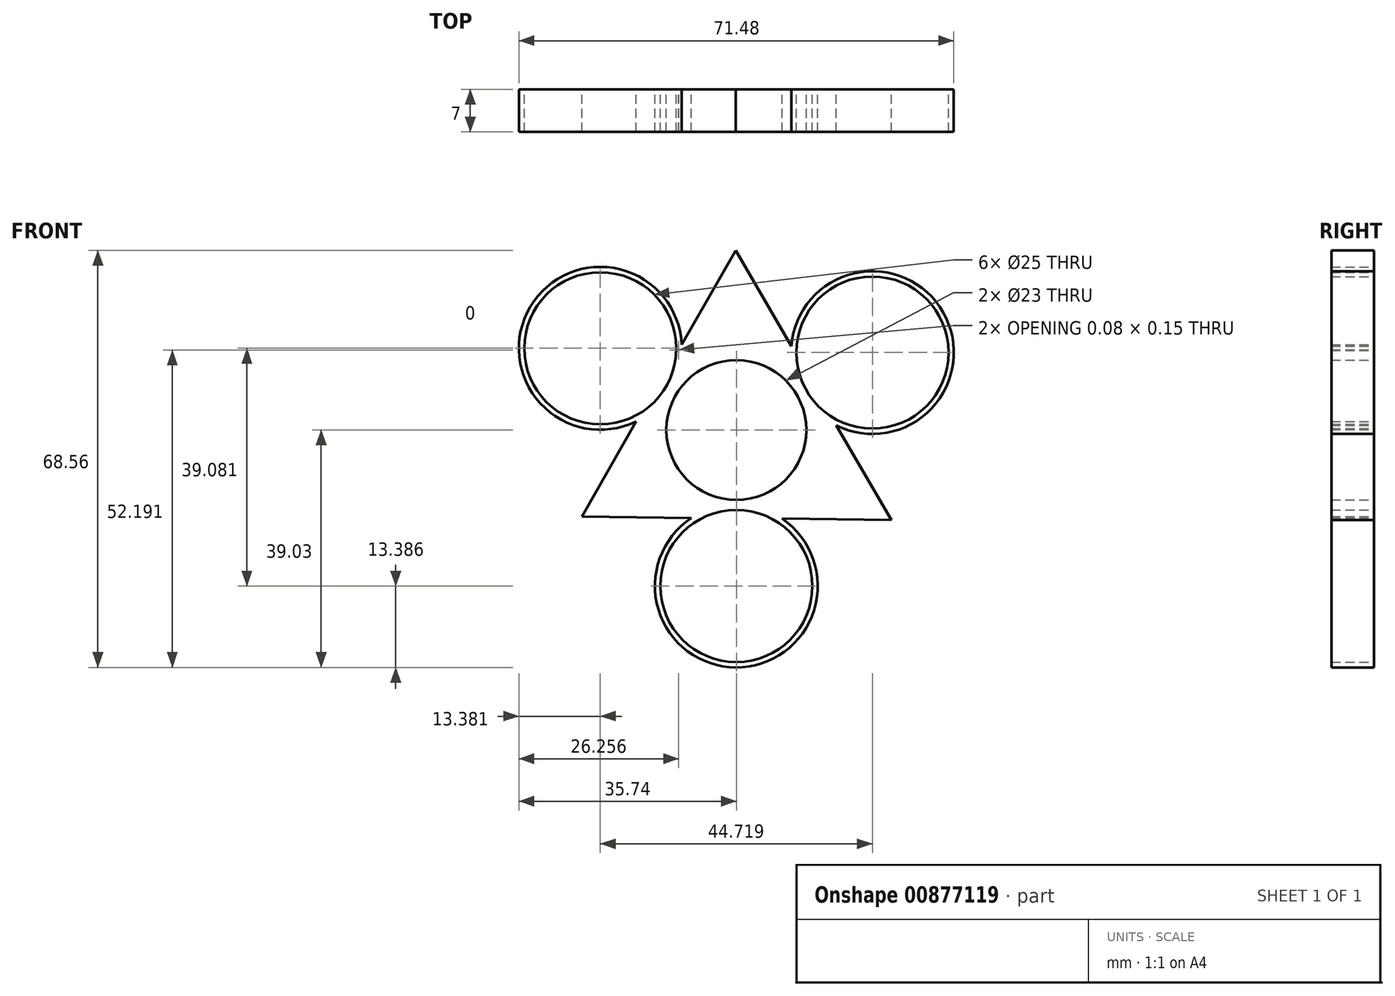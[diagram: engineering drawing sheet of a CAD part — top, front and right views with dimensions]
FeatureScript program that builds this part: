
annotation { "Feature Type Name" : "Feature", "Feature Type Description" : "" }
export const myFeature = defineFeature(function(context is Context, id is Id, definition is map)
    precondition{}
    {
        {
            var Q0;
            Q0=qCreatedBy(makeId("Front.planeOp"),FACE);
            var sketch = newSketch(context, id + "F0", { "sketchPlane" : qUnion([Q0])});
            skPoint(sketch, "E0.0.midPoint", {"position": v(-1.03, 12.4) * mm});
            skPoint(sketch, "E1.orphan", {"position": v(-18.38, 13.22) * mm});
            skPoint(sketch, "E0.0.start.orphan", {"position": v(16.32, 11.57) * mm});
            skCircle(sketch, "E2", {"center": v(0, 0) * mm, "radius": 11.5 * mm});
            skPoint(sketch, "E3.0.midPoint", {"position": v(21.95, 0) * mm});
            skPoint(sketch, "E4.orphan", {"position": v(21.95, 38.02) * mm});
            skPoint(sketch, "E3.0.end.orphan", {"position": v(21.95, -38.02) * mm});
            skPoint(sketch, "E5.0.midPoint", {"position": v(-12.82, 7.67) * mm});
            skPoint(sketch, "E5.1.start.orphan", {"position": v(0.46, 29.87) * mm});
            skPoint(sketch, "E5.0.start.orphan", {"position": v(-26.1, -14.53) * mm});
            skSolve(sketch);
        }
        {
            var Q0;
            Q0=qCreatedBy(makeId("Front.planeOp"),FACE);
            var sketch = newSketch(context, id + "F1", { "sketchPlane" : qUnion([Q0])});
            skPoint(sketch, "E6.0.midPoint", {"position": v(0, 3.19) * mm});
            skPoint(sketch, "E7.orphan", {"position": v(-16.3, -47.78) * mm});
            skPoint(sketch, "E6.1.start.orphan", {"position": v(16.3, 54.15) * mm});
            skPoint(sketch, "E8.orphan", {"position": v(16.3, -28.22) * mm});
            skPoint(sketch, "E6.cCircle.center.orphan", {"position": v(0, 0) * mm});
            skPoint(sketch, "E9.0.midPoint", {"position": v(20.45, 12.84) * mm});
            skPoint(sketch, "E10.center.orphan", {"position": v(40.9, -48.55) * mm});
            skPoint(sketch, "E11.orphan", {"position": v(-0.12, 29.53) * mm});
            skPoint(sketch, "E12.0.midPoint", {"position": v(0, 13.09) * mm});
            skLineSegment(sketch, "E13", {"start": v(122.5, 32.06) * mm, "end": v(120.9, 14.13) * mm});
            skLineSegment(sketch, "E14.0", {"start": v(-22.36, 13.44) * mm, "end": v(22.36, 12.73) * mm});
            skLineSegment(sketch, "E14.1", {"start": v(22.36, 12.73) * mm, "end": v(0, -25.64) * mm});
            skLineSegment(sketch, "E14.2", {"start": v(0, -25.64) * mm, "end": v(-15.98, 2.3) * mm});
            skLineSegment(sketch, "E15", {"start": v(-22.36, 13.44) * mm, "end": v(-15.98, 2.3) * mm});
            skPoint(sketch, "E16.first.point", {"position": v(-47.98, 64.64) * mm});
            skPoint(sketch, "E16.second.point", {"position": v(-35.77, 48.96) * mm});
            skPoint(sketch, "E16.third.point", {"position": v(-64.88, 40.62) * mm});
            skArc(sketch, "E17", {"start": v(-9.53, 13.09) * mm, "mid": v(-9.53, 13.16) * mm, "end": v(-9.52, 13.24) * mm});
            skPoint(sketch, "E18", {"position": v(15.9, 1.64) * mm});
            skPoint(sketch, "E19", {"position": v(6.46, -14.55) * mm});
            skCircle(sketch, "E20", {"center": v(-22.36, 13.44) * mm, "radius": 12.5 * mm});
            skCircle(sketch, "E21", {"center": v(0, -25.64) * mm, "radius": 12.5 * mm});
            skCircle(sketch, "E22", {"center": v(22.36, 12.73) * mm, "radius": 12.5 * mm});
            skLineSegment(sketch, "E23", {"start": v(-9.53, 13.09) * mm, "end": v(-0.12, 29.53) * mm});
            skLineSegment(sketch, "E24", {"start": v(-0.12, 29.53) * mm, "end": v(9.52, 12.94) * mm});
            skLineSegment(sketch, "E25", {"start": v(-15.98, 2.3) * mm, "end": v(-25.4, -14.24) * mm});
            skLineSegment(sketch, "E26", {"start": v(-25.4, -14.24) * mm, "end": v(-6.37, -14.5) * mm});
            skLineSegment(sketch, "E27", {"start": v(6.46, -14.55) * mm, "end": v(25.49, -14.79) * mm});
            skLineSegment(sketch, "E28", {"start": v(25.49, -14.79) * mm, "end": v(15.9, 1.64) * mm});
            skCircle(sketch, "E29", {"center": v(0, -25.64) * mm, "radius": 13.39 * mm});
            skCircle(sketch, "E30", {"center": v(-22.36, 13.44) * mm, "radius": 13.39 * mm});
            skCircle(sketch, "E31", {"center": v(22.36, 12.73) * mm, "radius": 13.39 * mm});
            skSolve(sketch);
        }
        {
            var Q0;
            Q0 = qSketchRegion(id + "F1", true);
            var Q1;
            {var subQ11=sQuery(id+"F1.wireOp",EDGE,"E17");Q1=makeQuery(id+"F1.imprint","IMPRINT",FACE,{"disambiguationData":[TD([[makeQuery(id+"F1.imprint","IMPRINT",EDGE,{"derivedFrom":subQ11}),1.0]])]});}
            var Q2;
            {var subQ4=sQuery(id+"F1.wireOp",EDGE,"E14.1");var subQ5=makeQuery(id+"F1.imprint","INTERSECT",VERTEX,{"derivedFrom":[subQ4,sQuery(id+"F1.wireOp",EDGE,"E27")]});Q2=makeQuery(id+"F1.imprint","IMPRINT",FACE,{"disambiguationData":[TD([[makeQuery(id+"F1.imprint","IMPRINT",EDGE,{"disambiguationData":[TD([[subQ5,1.0]])],"derivedFrom":subQ4}),-1.0]])]});}
            var Q3;
            {var subQ5=sQuery(id+"F1.wireOp",EDGE,"E30");var subQ8=sQuery(id+"F1.wireOp",EDGE,"E14.0");var subQ11=makeQuery(id+"F1.imprint","INTERSECT",VERTEX,{"derivedFrom":[subQ8,subQ5]});Q3=makeQuery(id+"F1.imprint","IMPRINT",FACE,{"disambiguationData":[TD([[makeQuery(id+"F1.imprint","IMPRINT",EDGE,{"disambiguationData":[TD([[subQ11,-1.0]])],"derivedFrom":subQ8}),-1.0]])]});}
            var Q4;
            {var subQ4=sQuery(id+"F1.wireOp",EDGE,"E14.0");var subQ5=makeQuery(id+"F1.imprint","INTERSECT",VERTEX,{"derivedFrom":[subQ4,sQuery(id+"F1.wireOp",EDGE,"E24")]});Q4=makeQuery(id+"F1.imprint","IMPRINT",FACE,{"disambiguationData":[TD([[makeQuery(id+"F1.imprint","IMPRINT",EDGE,{"disambiguationData":[TD([[subQ5,1.0]])],"derivedFrom":subQ4}),-1.0]])]});}
            extrude(context, id + "F2", {"entities" : qUnion([Q0, Q1, Q2, Q3, Q4]), "depth" : 7 * mm, "offsetDistance" : 25.4 * mm});
        }
        {
            var Q0;
            Q0 = qSketchRegion(id + "F0", true);
            extrude(context, id + "F3", {"entities" : qUnion([Q0]), "operationType" : NewBodyOperationType.REMOVE, "depth" : 26.42 * mm, "offsetDistance" : 25.4 * mm});
        }
    });
